# Revit family: Thorn GTLED PRO
name_source: partatom
category: Lighting Fixtures
revit_build: Autodesk Revit 2016 (Build: 20150220_1215(x64)
units: mm (PartAtom-declared; Revit-internal decimal feet)

## family parameters
Cut with Voids When Loaded = No
Host = Face
Light Source = Yes
OmniClass Number = 23.80.70.11
OmniClass Title = Luminaries for Internal Lighting
Part Type = Normal
Room Calculation Point = No
Round Connector Dimension = Use Diameter
Shared = No

## types (4) — shared parameters
Assembly Code = D5020200
Body = Thorn_Metal_Light_Grey
Color Filter = 16777215
Cover = Thorn_PMMA
Description = Ceiling LED luminaire
Dimming Lamp Color Temperature Shift = <None>
Emit Shape Visible in Rendering = No
Lamp = LED
Manufacturer = Thorn Lighting
Tilt Angle = -90.00°
Voltage = 230 V
zero-valued in all types: Default Elevation

## per-type parameters (varying)
| type | Apparent Load | Emit from Rectangle Length | Emit from Rectangle Width | Height | Length | Model | Photometric Web File | URL | Width |
| GP-S | 71 VA | 88 mm | 613 mm | 84 mm  [stored 0.275591 ft] | 773 mm  [stored 2.53609 ft] | 96276235 | GP-S.IES | www.thornlighting.com/96276235 | 168 mm  [stored 0.551181 ft] |
| GP-M | 102 VA | 233 mm | 640 mm  [stored 2.09974 ft] | 90 mm  [stored 0.295276 ft] | 800 mm  [stored 2.62467 ft] | 96276619 | GP-M.IES | www.thornlighting.com/96276619 | 313 mm  [stored 1.0269 ft] |
| GP-L | 140 VA | 233 mm | 792 mm  [stored 2.59843 ft] | 90 mm  [stored 0.295276 ft] | 952 mm  [stored 3.12336 ft] | 96276374 | GP-L.IES | www.thornlighting.com/96276374 | 313 mm  [stored 1.0269 ft] |
| GP-XL | 210 VA | 233 mm | 1160 mm | 90 mm  [stored 0.295276 ft] | 1320 mm | 96276379 | GP-XL.IES | www.thornlighting.com/96276379 | 313 mm  [stored 1.0269 ft] |

note: [stored X ft] marks values corroborated as IEEE doubles in the binary element streams (Revit-internal decimal feet)

## geometry (parser evidence)
native form markers: Sweep x3
no freeform markers — native parametric forms only
